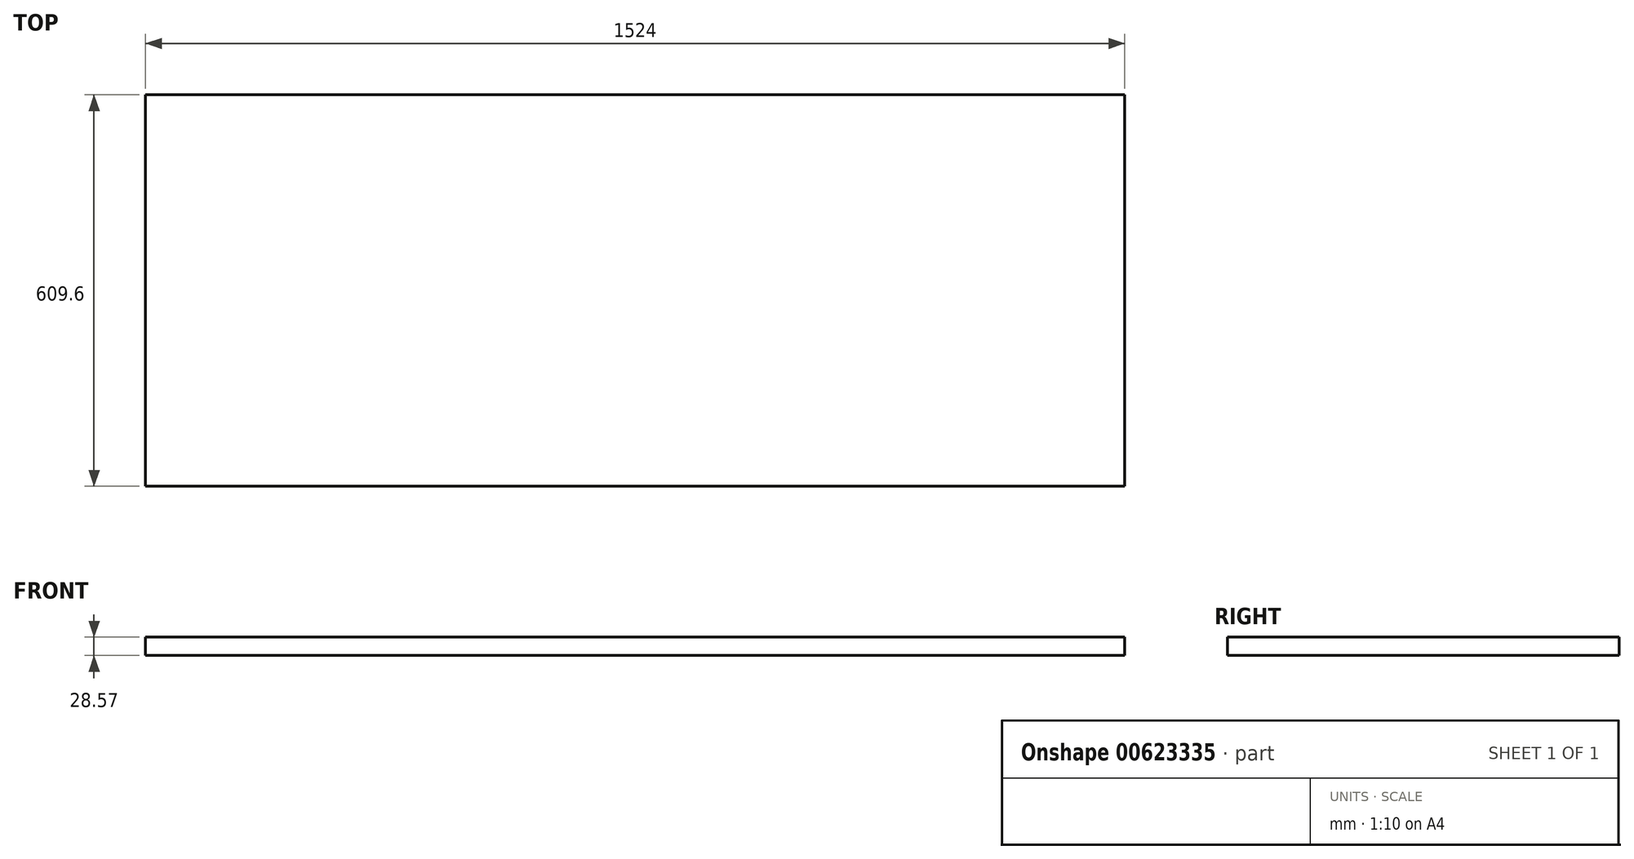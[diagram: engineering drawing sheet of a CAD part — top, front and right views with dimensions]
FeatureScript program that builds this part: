
annotation { "Feature Type Name" : "Feature", "Feature Type Description" : "" }
export const myFeature = defineFeature(function(context is Context, id is Id, definition is map)
    precondition{}
    {
        {
            var Q0;
            Q0=qCreatedBy(makeId("Top.planeOp"),FACE);
            var sketch = newSketch(context, id + "F0", { "sketchPlane" : qUnion([Q0])});
            skLineSegment(sketch, "E0.bottom", {"start": v(762, 304.8) * mm, "end": v(-762, 304.8) * mm});
            skLineSegment(sketch, "E0.top", {"start": v(762, -304.8) * mm, "end": v(-762, -304.8) * mm});
            skLineSegment(sketch, "E0.left", {"start": v(762, 304.8) * mm, "end": v(762, -304.8) * mm});
            skLineSegment(sketch, "E0.right", {"start": v(-762, 304.8) * mm, "end": v(-762, -304.8) * mm});
            skPoint(sketch, "E0.middle", {"position": v(0, 0) * mm});
            skSolve(sketch);
        }
        {
            var Q0;
            Q0=makeQuery(id+"F0.imprint","IMPRINT",FACE,{"disambiguationData":[TD([[makeQuery(id+"F0.imprint","IMPRINT",EDGE,{"derivedFrom":sQuery(id+"F0.wireOp",EDGE,"E0.bottom")}),1.0]])]});
            extrude(context, id + "F1", {"entities" : qUnion([Q0]), "depth" : 28.57 * mm, "offsetDistance" : 25.4 * mm});
        }
    });
